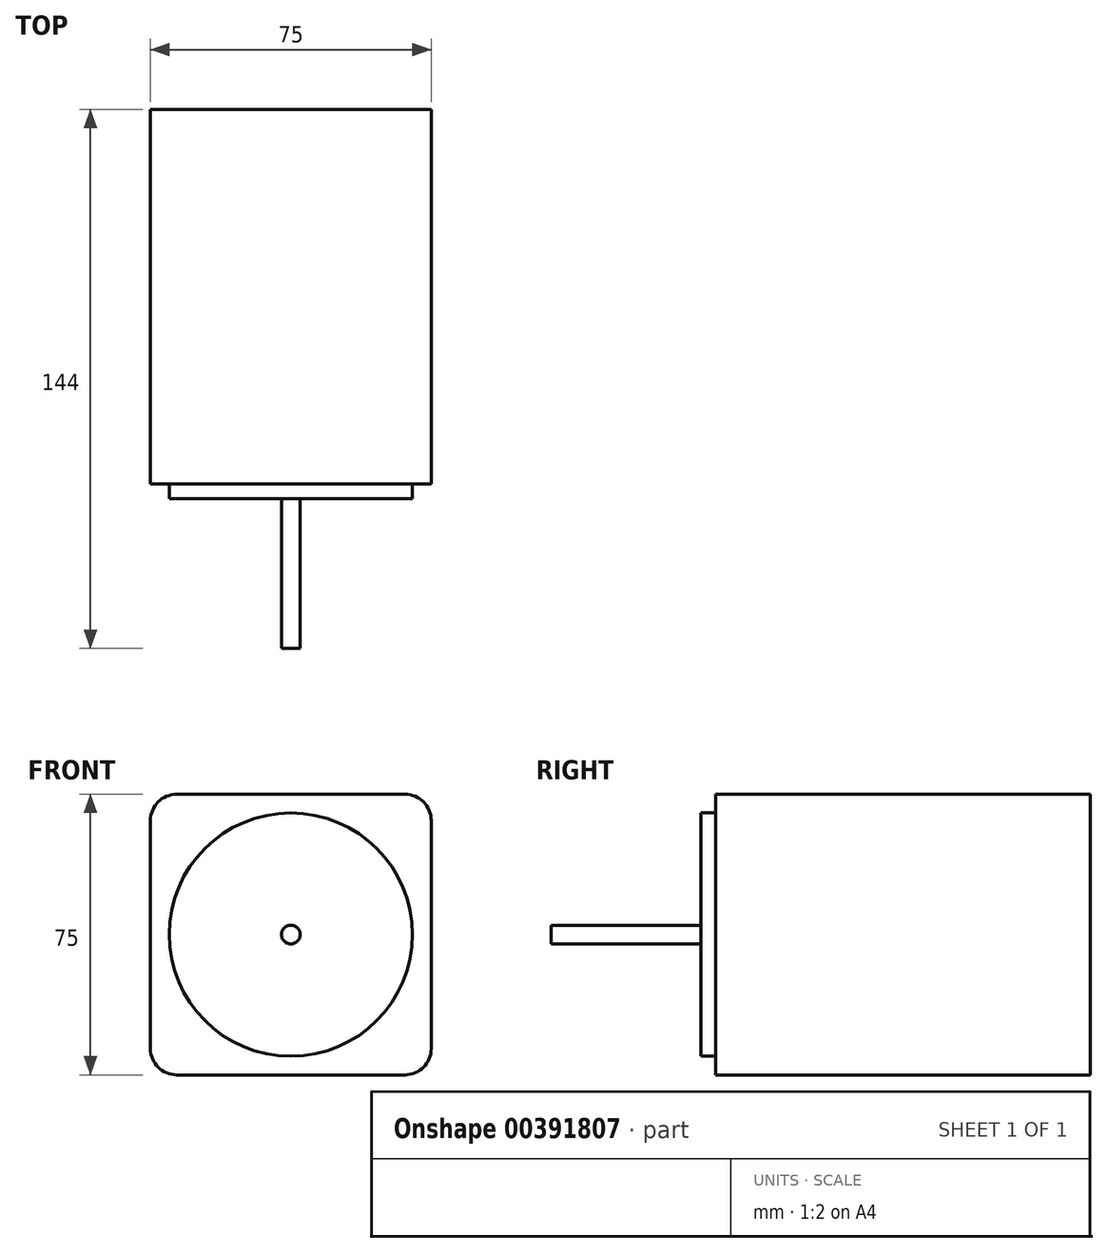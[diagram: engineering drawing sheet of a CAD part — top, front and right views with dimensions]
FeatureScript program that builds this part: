
annotation { "Feature Type Name" : "Feature", "Feature Type Description" : "" }
export const myFeature = defineFeature(function(context is Context, id is Id, definition is map)
    precondition{}
    {
        {
            var Q0;
            Q0=qCreatedBy(makeId("Front.planeOp"),FACE);
            var sketch = newSketch(context, id + "F0", { "sketchPlane" : qUnion([Q0])});
            skLineSegment(sketch, "E0.bottom", {"start": v(37.5, 37.5) * mm, "end": v(-37.5, 37.5) * mm});
            skLineSegment(sketch, "E0.top", {"start": v(37.5, -37.5) * mm, "end": v(-37.5, -37.5) * mm});
            skLineSegment(sketch, "E0.left", {"start": v(37.5, 37.5) * mm, "end": v(37.5, -37.5) * mm});
            skLineSegment(sketch, "E0.right", {"start": v(-37.5, 37.5) * mm, "end": v(-37.5, -37.5) * mm});
            skPoint(sketch, "E0.middle", {"position": v(0, 0) * mm});
            skSolve(sketch);
        }
        {
            var Q0;
            Q0=makeQuery(id+"F0.imprint","IMPRINT",FACE,{"disambiguationData":[TD([[makeQuery(id+"F0.imprint","IMPRINT",EDGE,{"derivedFrom":sQuery(id+"F0.wireOp",EDGE,"E0.bottom")}),1.0]])]});
            extrude(context, id + "F1", {"entities" : qUnion([Q0]), "oppositeDirection" : true, "depth" : 100 * mm});
        }
        {
            var Q0;
            Q0=makeQuery(id+"F1.opExtrude","SWEPT_EDGE",EDGE,{"disambiguationData":[OSD([sQuery(id+"F0.wireOp",EDGE,"E0.bottom"),sQuery(id+"F0.wireOp",EDGE,"E0.left")])]});
            var Q1;
            Q1=makeQuery(id+"F1.opExtrude","SWEPT_EDGE",EDGE,{"disambiguationData":[OSD([sQuery(id+"F0.wireOp",EDGE,"E0.top"),sQuery(id+"F0.wireOp",EDGE,"E0.left")])]});
            var Q2;
            Q2=makeQuery(id+"F1.opExtrude","SWEPT_EDGE",EDGE,{"disambiguationData":[OSD([sQuery(id+"F0.wireOp",EDGE,"E0.top"),sQuery(id+"F0.wireOp",EDGE,"E0.right")])]});
            var Q3;
            Q3=makeQuery(id+"F1.opExtrude","SWEPT_EDGE",EDGE,{"disambiguationData":[OSD([sQuery(id+"F0.wireOp",EDGE,"E0.bottom"),sQuery(id+"F0.wireOp",EDGE,"E0.right")])]});
            fillet(context, id + "F2", {"entities" : qUnion([Q0, Q1, Q2, Q3]), "radius" : 7 * mm, "tangentPropagation" : true, "allowEdgeOverflow" : false});
        }
        {
            var Q0;
            Q0=makeQuery(id+"F1.opExtrude","CAP_FACE",FACE,{"disambiguationData":[OSD([sQuery(id+"F0.wireOp",EDGE,"E0.bottom"),sQuery(id+"F0.wireOp",EDGE,"E0.top"),sQuery(id+"F0.wireOp",EDGE,"E0.left"),sQuery(id+"F0.wireOp",EDGE,"E0.right")])],"isStart":true});
            var sketch = newSketch(context, id + "F3", { "sketchPlane" : qUnion([Q0])});
            skCircle(sketch, "E1", {"center": v(0, 0) * mm, "radius": 32.5 * mm});
            skSolve(sketch);
        }
        {
            var Q0;
            Q0=makeQuery(id+"F3.imprint","IMPRINT",FACE,{"disambiguationData":[TD([[makeQuery(id+"F3.imprint","IMPRINT",EDGE,{"derivedFrom":sQuery(id+"F3.wireOp",EDGE,"E1")}),1.0]])]});
            extrude(context, id + "F4", {"entities" : qUnion([Q0]), "operationType" : NewBodyOperationType.ADD, "depth" : 4 * mm});
        }
        {
            var Q0;
            Q0=makeQuery(id+"F4.opExtrude","CAP_FACE",FACE,{"disambiguationData":[OSD([sQuery(id+"F3.wireOp",EDGE,"E1")])],"isStart":false});
            var sketch = newSketch(context, id + "F5", { "sketchPlane" : qUnion([Q0])});
            skCircle(sketch, "E2", {"center": v(0, 0) * mm, "radius": 2.5 * mm});
            skSolve(sketch);
        }
        {
            var Q0;
            Q0=makeQuery(id+"F5.imprint","IMPRINT",FACE,{"disambiguationData":[TD([[makeQuery(id+"F5.imprint","IMPRINT",EDGE,{"derivedFrom":sQuery(id+"F5.wireOp",EDGE,"E2")}),1.0]])]});
            extrude(context, id + "F6", {"entities" : qUnion([Q0]), "operationType" : NewBodyOperationType.ADD, "depth" : 40 * mm});
        }
    });
